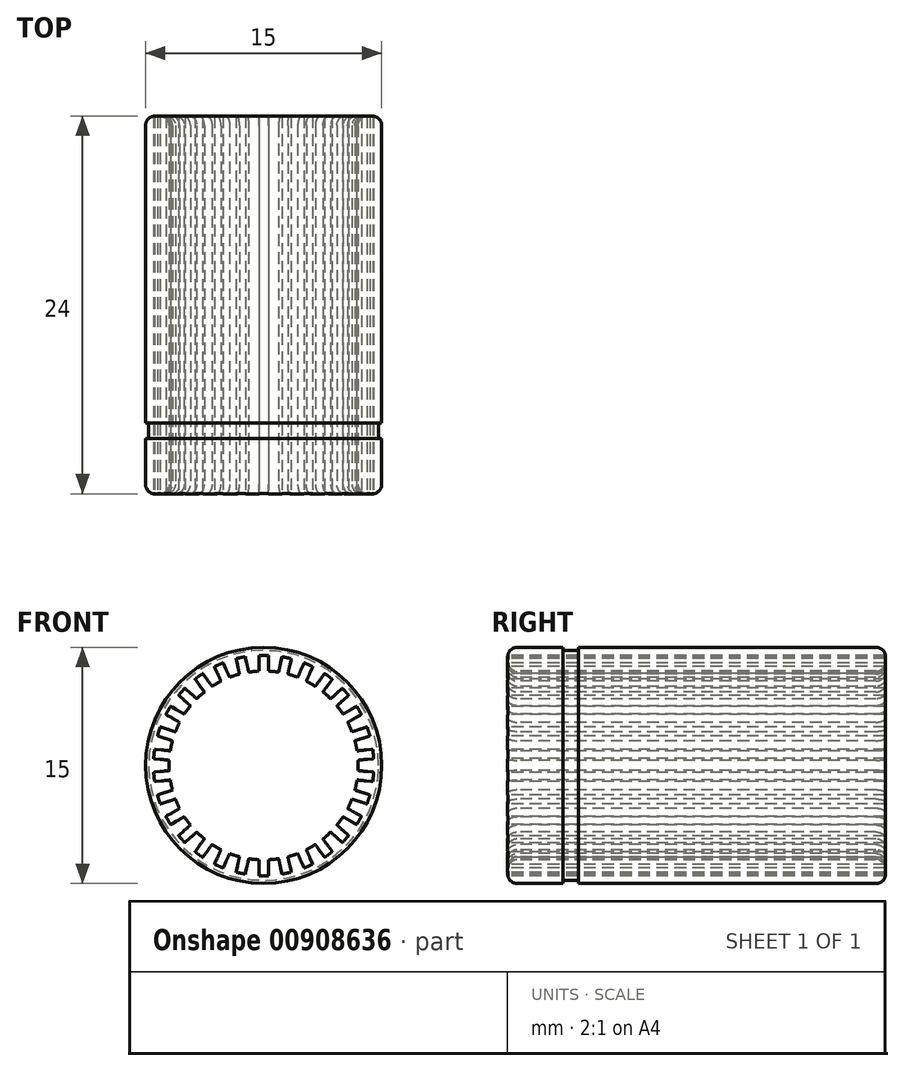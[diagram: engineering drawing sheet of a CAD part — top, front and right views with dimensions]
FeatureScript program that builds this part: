
annotation { "Feature Type Name" : "Feature", "Feature Type Description" : "" }
export const myFeature = defineFeature(function(context is Context, id is Id, definition is map)
    precondition{}
    {
        {
            var Q0;
            Q0=qCreatedBy(makeId("Front.planeOp"),FACE);
            var sketch = newSketch(context, id + "F0", { "sketchPlane" : qUnion([Q0])});
            skCircle(sketch, "E0", {"center": v(0, 0) * mm, "radius": 7.5 * mm});
            skCircle(sketch, "E1", {"center": v(0, 0) * mm, "radius": 6 * mm});
            skLineSegment(sketch, "E2", {"start": v(0, 7.5) * mm, "end": v(0, -7.5) * mm, "construction": true});
            skLineSegment(sketch, "E3", {"start": v(-7.5, 0) * mm, "end": v(7.5, 0) * mm, "construction": true});
            skSolve(sketch);
        }
        {
            var Q0;
            Q0=qSketchRegion(id+"F0",true);
            extrude(context, id + "F1", {"entities" : qUnion([Q0]), "endBound" : BoundingType.SYMMETRIC, "oppositeDirection" : true, "depth" : 24 * mm, "offsetDistance" : 25 * mm});
        }
        {
            var Q0;
            Q0=makeQuery(id+"F1.opExtrude","CAP_EDGE",EDGE,{"disambiguationData":[OSD([sQuery(id+"F0.wireOp",EDGE,"E1")])],"isStart":true});
            var Q1;
            Q1=makeQuery(id+"F1.opExtrude","CAP_EDGE",EDGE,{"disambiguationData":[OSD([sQuery(id+"F0.wireOp",EDGE,"E0")])],"isStart":true});
            var Q2;
            Q2=makeQuery(id+"F1.opExtrude","CAP_EDGE",EDGE,{"disambiguationData":[OSD([sQuery(id+"F0.wireOp",EDGE,"E1")])],"isStart":false});
            var Q3;
            Q3=makeQuery(id+"F1.opExtrude","CAP_EDGE",EDGE,{"disambiguationData":[OSD([sQuery(id+"F0.wireOp",EDGE,"E0")])],"isStart":false});
            fillet(context, id + "F2", {"entities" : qUnion([Q0, Q1, Q2, Q3]), "radius" : .6 * mm, "tangentPropagation" : true, "allowEdgeOverflow" : false});
        }
        {
            var Q0;
            Q0=qCreatedBy(makeId("Front.planeOp"),FACE);
            var sketch = newSketch(context, id + "F3", { "sketchPlane" : qUnion([Q0])});
            skLineSegment(sketch, "E4", {"start": v(0, 0) * mm, "end": v(0.3, 0) * mm});
            skLineSegment(sketch, "E5", {"start": v(0.3, 0) * mm, "end": v(0.3, 7) * mm});
            skLineSegment(sketch, "E6", {"start": v(0.3, 7) * mm, "end": v(-0.3, 7) * mm});
            skLineSegment(sketch, "E7", {"start": v(-0.3, 7) * mm, "end": v(-0.3, 0) * mm});
            skLineSegment(sketch, "E8", {"start": v(-0.3, 0) * mm, "end": v(0, 0) * mm});
            skLineSegment(sketch, "E9", {"start": v(0, 0) * mm, "end": v(0, 7) * mm, "construction": true});
            skPoint(sketch, "E10", {"position": v(0, 6) * mm});
            skCircle(sketch, "E11.0", {"center": v(0, 0) * mm, "radius": 6 * mm, "construction": true});
            skSolve(sketch);
        }
        {
            var Q0;
            Q0 = qSketchRegion(id + "F3", true);
            extrude(context, id + "F4", {"entities" : qUnion([Q0]), "operationType" : NewBodyOperationType.REMOVE, "endBound" : BoundingType.THROUGH_ALL, "oppositeDirection" : true, "depth" : 25 * mm, "offsetDistance" : 25 * mm, "hasSecondDirection" : true, "secondDirectionBound" : SecondDirectionBoundingType.THROUGH_ALL, "secondDirectionOppositeDirection" : false, "secondDirectionDepth" : 25 * mm});
        }
        {
            var Q0;
            Q0=qCreatedBy(makeId("Right.planeOp"),FACE);
            var sketch = newSketch(context, id + "F5", { "sketchPlane" : qUnion([Q0])});
            skLineSegment(sketch, "E12", {"start": v(-55.45, 0) * mm, "end": v(55.45, 0) * mm, "construction": true});
            skSolve(sketch);
        }
        {
            var Q0;
            Q0=makeQuery(id+"F4.boolean.opBoolean","COPY",FACE,{"derivedFrom":makeQuery(id+"F4.opExtrude","SWEPT_FACE",FACE,{"disambiguationData":[OSD([sQuery(id+"F3.wireOp",EDGE,"E7")])]})});
            var Q1;
            Q1=makeQuery(id+"F4.boolean.opBoolean","COPY",FACE,{"derivedFrom":makeQuery(id+"F4.opExtrude","SWEPT_FACE",FACE,{"disambiguationData":[OSD([sQuery(id+"F3.wireOp",EDGE,"E5")])]})});
            var Q2;
            Q2=makeQuery(id+"F4.boolean.opBoolean","COPY",FACE,{"derivedFrom":makeQuery(id+"F4.opExtrude","SWEPT_FACE",FACE,{"disambiguationData":[OSD([sQuery(id+"F3.wireOp",EDGE,"E6")])]})});
            var Q3;
            Q3=sQuery(id+"F5.wireOp",EDGE,"E12");
            circularPattern(context, id + "F6", {"patternType" : PatternType.FACE, "operationType" : NewBodyOperationType.REMOVE, "faces" : qUnion([Q0, Q1, Q2]), "axis" : qUnion([Q3]), "angle" : 360 * degree, "instanceCount" : 30, "equalSpace" : true});
        }
        {
            var Q0;
            Q0=qCreatedBy(makeId("Right.planeOp"),FACE);
            var sketch = newSketch(context, id + "F7", { "sketchPlane" : qUnion([Q0])});
            skLineSegment(sketch, "E13.bottom", {"start": v(-8.5, 7.5) * mm, "end": v(-7.5, 7.5) * mm});
            skLineSegment(sketch, "E13.top", {"start": v(-8.5, 7.3) * mm, "end": v(-7.5, 7.3) * mm});
            skLineSegment(sketch, "E13.left", {"start": v(-8.5, 7.5) * mm, "end": v(-8.5, 7.3) * mm});
            skLineSegment(sketch, "E13.right", {"start": v(-7.5, 7.5) * mm, "end": v(-7.5, 7.3) * mm});
            skLineSegment(sketch, "E14", {"start": v(-11.4, 7.5) * mm, "end": v(11.4, 7.5) * mm, "construction": true});
            skLineSegment(sketch, "E15", {"start": v(-16.58, 0) * mm, "end": v(16.95, 0) * mm, "construction": true});
            skSolve(sketch);
        }
        {
            var Q0;
            Q0 = qSketchRegion(id + "F7", true);
            var Q1;
            Q1=sQuery(id+"F7.wireOp",EDGE,"E15");
            revolve(context, id + "F8", {"operationType" : NewBodyOperationType.REMOVE, "surfaceOperationType" : NewSurfaceOperationType.NEW, "entities" : qUnion([Q0]), "axis" : qUnion([Q1]), "revolveType" : RevolveType.FULL, "oppositeDirection" : true});
        }
    });
